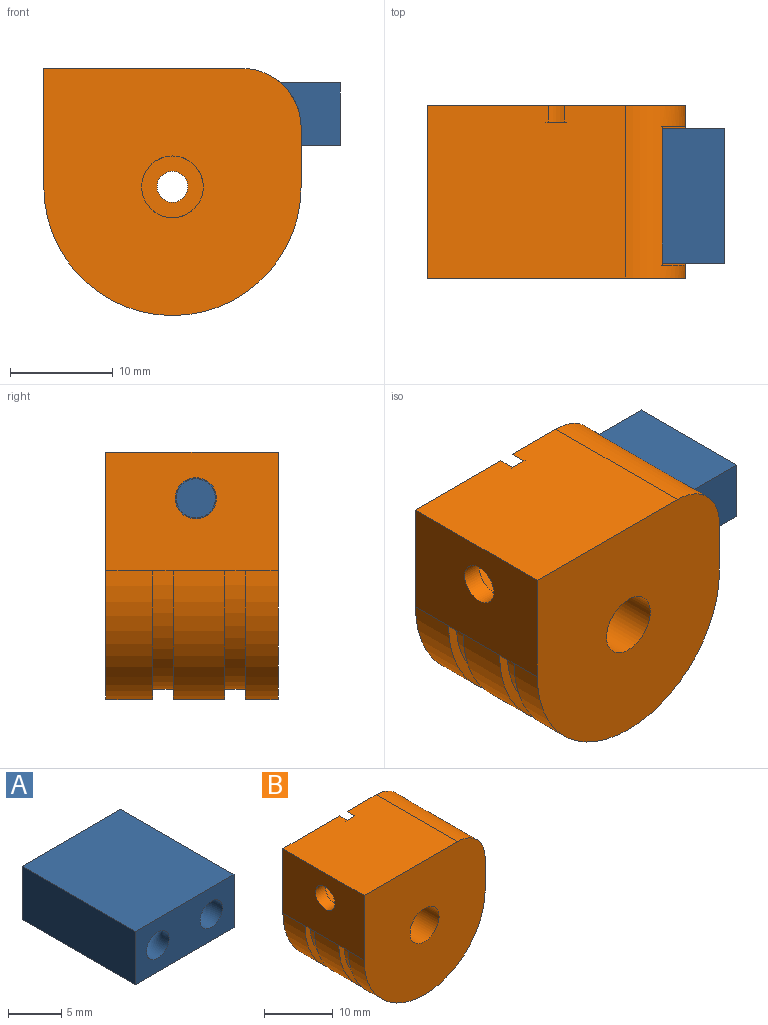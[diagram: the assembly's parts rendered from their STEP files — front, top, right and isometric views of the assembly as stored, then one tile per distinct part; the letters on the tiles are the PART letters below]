
ASSEMBLY  parts=2 mates=1
PART A: 9 faces, bbox 13.1x15x6.1 mm
  f0: plane 15x13.1mm, normal (0,0,-1), area 196.5mm2, adj f1,f3,f4,f7
  f1: plane 15x6.1mm, normal (1,0,0), area 91.5mm2, adj f0,f2,f4,f7
  f2: plane 15x13.1mm, normal (0,0,1), area 196.5mm2, adj f1,f3,f4,f7
  f3: plane 15x6.1mm, normal (-1,0,0), area 91.5mm2, adj f0,f2,f4,f7
  f4: plane 13.1x6.1mm, normal (0,1,0), area 68.6mm2, adj f0,f1,f2,f3,f5
  f5: cylinder r=1.9mm len=9mm, axis (0,1,0), area 107.4mm2, adj f4,f6
  f6: plane 3.8x3.8mm, normal (0,1,0), area 11.3mm2, adj f5
  f7: plane 13.1x6.1mm, normal (0,-1,0), area 65.8mm2, adj f0,f1,f2,f3,f8
  f8: torus R=3.55mm, axis (0,0,-1), area 105.1mm2, adj f7
PART B: 54 faces, bbox 25x16.8x24 mm
  f0: cylinder r=3mm len=13.55mm, axis (0,1,0), area 255.4mm2, adj f11,f50
  f1: plane 19.25x16.75mm, normal (0,0,1), area 319.9mm2, adj f8,f10,f11,f27,f31,f32,f33
  f2: cylinder r=3.6mm len=7.2mm, axis (0,1,0), area 13.6mm2, adj f30,f33
  f3: plane 5x3.8mm, normal (1,0,0), area 19mm2, adj f4,f12,f17,f24
  f4: cylinder r=12.5mm len=25mm, axis (0,1,0), area 196.3mm2, adj f3,f10,f17,f24
  f5: plane 5.75x4.55mm, normal (1,0,0), area 21.2mm2, adj f6,f8,f12,f13,f18,f27
  f6: cylinder r=12.5mm len=25mm, axis (0,1,0), area 178.7mm2, adj f5,f10,f18,f27
  f7: plane 5.75x3.2mm, normal (1,0,0), area 14.6mm2, adj f8,f9,f11,f12,f14,f23
  f8: cylinder r=5.75mm len=16.75mm, axis (0,1,0), area 80.4mm2, adj f1,f5,f7,f11,f13,f14,f15,f27
  f9: cylinder r=12.5mm len=25mm, axis (0,1,0), area 125.7mm2, adj f7,f10,f11,f23
  f10: plane 16.75x11.5mm, normal (-1,0,0), area 180.1mm2, adj f1,f4,f6,f9,f11,f21,f26,f27
  f11: plane 25x24mm, normal (0,-1,0), area 497.6mm2, adj f0,f1,f7,f8,f9,f10
  f12: plane 23x13.5mm, normal (0,0,1), area 302.5mm2, adj f3,f5,f7,f13,f14,f16,f17,f18
  f13: plane 23x6.5mm, normal (0,-1,0), area 146.4mm2, adj f5,f8,f12,f15,f16
  f14: plane 23x6.5mm, normal (0,1,0), area 146.4mm2, adj f7,f8,f12,f15,f16
  f15: plane 20.77x13.5mm, normal (0,0,-1), area 280.3mm2, adj f8,f13,f14,f16
  f16: plane 13.5x6.5mm, normal (1,0,0), area 75.2mm2, adj f12,f13,f14,f15,f53
  f17: plane 25x16.3mm, normal (0,1,0), area 41.7mm2, adj f3,f4,f12,f19,f20,f21,f29
  f18: plane 25x16.3mm, normal (0,-1,0), area 41.7mm2, adj f5,f6,f12,f19,f20,f21,f29
  f19: plane 2.8x2mm, normal (1,0,0), area 5.6mm2, adj f17,f18,f20,f29
  f20: cylinder r=11.5mm len=23mm, axis (0,1,0), area 72.3mm2, adj f17,f18,f19,f21
  f21: plane 2x1mm, normal (0,0,-1), area 2mm2, adj f10,f17,f18,f20
  f22: plane 2.8x2mm, normal (1,0,0), area 5.6mm2, adj f23,f24,f25,f28
  f23: plane 25x16.3mm, normal (0,1,0), area 41.7mm2, adj f7,f9,f12,f22,f25,f26,f28
  f24: plane 25x16.3mm, normal (0,-1,0), area 41.7mm2, adj f3,f4,f12,f22,f25,f26,f28
  f25: cylinder r=11.5mm len=23mm, axis (0,1,0), area 72.3mm2, adj f22,f23,f24,f26
  f26: plane 2x1mm, normal (0,0,-1), area 2mm2, adj f10,f23,f24,f25
  f27: plane 25x24mm, normal (0,1,0), area 293.2mm2, adj f1,f5,f6,f8,f10,f31,f32,f34
  f28: cylinder r=1mm len=2mm, axis (0,1,0), area 3.1mm2, adj f12,f22,f23,f24
  f29: cylinder r=1mm len=2mm, axis (0,1,0), area 3.1mm2, adj f12,f17,f18,f19
  f30: plane 7.2x7.2mm, normal (0,1,0), area 14.3mm2, adj f2,f51
  f31: cylinder r=3.1mm len=3mm, axis (0,1,0), area 6.5mm2, adj f1,f27,f33,f48
  f32: cylinder r=3.1mm len=3mm, axis (0,1,0), area 6.5mm2, adj f1,f27,f33,f34
  f33: plane 23.2x23.1mm, normal (0,1,0), area 192mm2, adj f1,f2,f31,f32,f34,f35,f36,f37
  f34: plane 5.24x1.6mm, normal (-1,0,0), area 8.4mm2, adj f27,f32,f33,f35
  f35: cylinder r=4.5mm len=1.6mm, axis (0,1,0), area 0.4mm2, adj f27,f33,f34,f36
  f36: plane 5.24x1.6mm, normal (0,0,-1), area 8.4mm2, adj f27,f33,f35,f37
  f37: cylinder r=3.1mm len=6.2mm, axis (0,1,0), area 15.6mm2, adj f27,f33,f36,f38
  f38: plane 5.24x1.6mm, normal (0,0,1), area 8.4mm2, adj f27,f33,f37,f39
  f39: cylinder r=4.5mm len=1.6mm, axis (0,1,0), area 0.4mm2, adj f27,f33,f38,f40
  f40: plane 5.24x1.6mm, normal (-1,0,0), area 8.4mm2, adj f27,f33,f39,f41
  f41: cylinder r=3.1mm len=6.2mm, axis (0,1,0), area 15.6mm2, adj f27,f33,f40,f42
  f42: plane 5.24x1.6mm, normal (1,0,0), area 8.4mm2, adj f27,f33,f41,f43
  f43: cylinder r=4.5mm len=1.6mm, axis (0,1,0), area 0.4mm2, adj f27,f33,f42,f44
  f44: plane 5.24x1.6mm, normal (0,0,1), area 8.4mm2, adj f27,f33,f43,f45
  f45: cylinder r=3.1mm len=6.2mm, axis (0,1,0), area 15.6mm2, adj f27,f33,f44,f46
  f46: plane 5.24x1.6mm, normal (0,0,-1), area 8.4mm2, adj f27,f33,f45,f47
  f47: cylinder r=4.5mm len=1.6mm, axis (0,1,0), area 0.4mm2, adj f27,f33,f46,f48
  f48: plane 5.24x1.6mm, normal (1,0,0), area 8.4mm2, adj f27,f31,f33,f47
  f49: cylinder r=1.5mm len=3mm, axis (0,1,0), area 14.1mm2, adj f50,f52
  f50: plane 6x6mm, normal (0,-1,0), area 21.2mm2, adj f0,f49
  f51: cylinder r=2.9mm len=5.8mm, axis (0,-1,0), area 9.1mm2, adj f30,f52
  f52: plane 5.8x5.8mm, normal (0,1,0), area 19.4mm2, adj f49,f51
  f53: cylinder r=2mm len=4mm, axis (-1,0,0), area 25.1mm2, adj f10,f16
PLACE A rot(axis=(0,0,1),90deg) t=(1.3,-8.75,7.05)mm
PLACE B at identity
MATE slider A.f5 <-> B.f53  axis (-1,0,0) through (1.3,-8.75,7.05)mm
